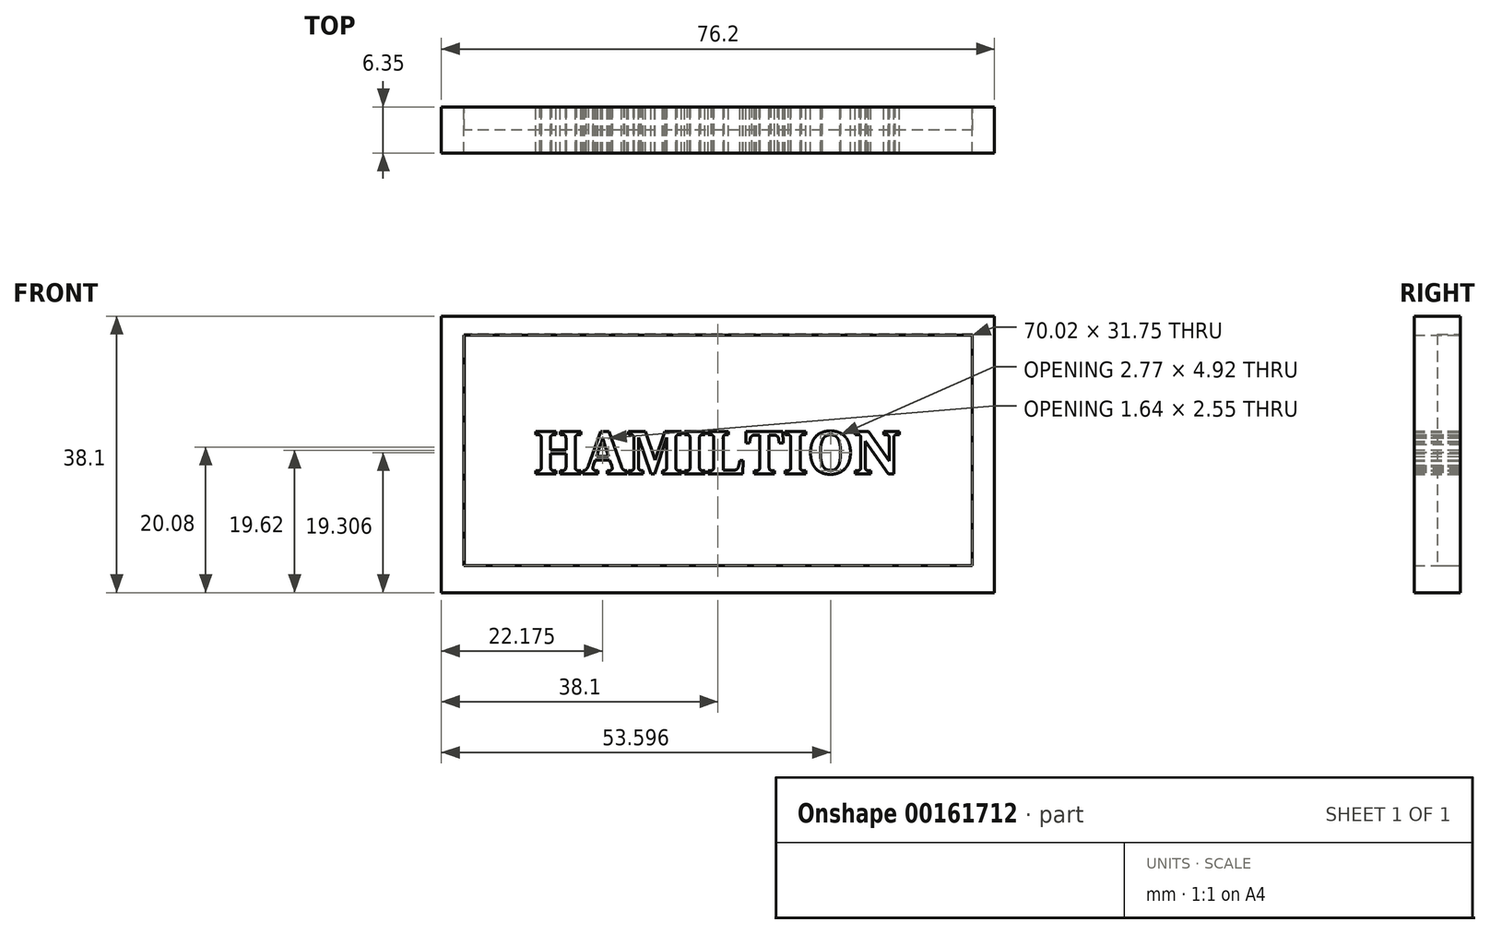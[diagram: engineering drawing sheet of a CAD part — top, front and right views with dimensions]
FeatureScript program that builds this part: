
annotation { "Feature Type Name" : "Feature", "Feature Type Description" : "" }
export const myFeature = defineFeature(function(context is Context, id is Id, definition is map)
    precondition{}
    {
        {
            var Q0;
            Q0=qCreatedBy(makeId("Front.planeOp"),FACE);
            var sketch = newSketch(context, id + "F0", { "sketchPlane" : qUnion([Q0])});
            skLineSegment(sketch, "E0.bottom", {"start": v(38.1, 19.05) * mm, "end": v(-38.1, 19.05) * mm});
            skLineSegment(sketch, "E0.top", {"start": v(38.1, -19.05) * mm, "end": v(-38.1, -19.05) * mm});
            skLineSegment(sketch, "E0.left", {"start": v(38.1, 19.05) * mm, "end": v(38.1, -19.05) * mm});
            skLineSegment(sketch, "E0.right", {"start": v(-38.1, 19.05) * mm, "end": v(-38.1, -19.05) * mm});
            skPoint(sketch, "E0.middle", {"position": v(0, 0) * mm});
            skText(sketch, "E1", { "text": "HAMILTION", "fontName": "NotoSerif-Bold.ttf"});
            skLineSegment(sketch, "E2.bottom", {"start": v(-35.01, 16.44) * mm, "end": v(35.01, 16.44) * mm});
            skLineSegment(sketch, "E2.top", {"start": v(-35.01, -15.3) * mm, "end": v(35.01, -15.3) * mm});
            skLineSegment(sketch, "E2.left", {"start": v(-35.01, 16.44) * mm, "end": v(-35.01, -15.3) * mm});
            skLineSegment(sketch, "E2.right", {"start": v(35.01, 16.44) * mm, "end": v(35.01, -15.3) * mm});
            skCircle(sketch, "E3", {"center": v(-30.43, 12.8) * mm, "radius": 2.29 * mm});
            skPoint(sketch, "E3.first.point", {"position": v(-32.08, 14.39) * mm});
            skPoint(sketch, "E3.second.point", {"position": v(-29.14, 10.9) * mm});
            skPoint(sketch, "E3.third.point", {"position": v(-30.06, 10.54) * mm});
            const initialGuessF0  = {"E1": [-0.02534, -0.00265, 1, 0, 0.00585]};
            skSetInitialGuess(sketch, initialGuessF0);
            skSolve(sketch);
        }
        {
            var Q0;
            Q0=makeQuery(id+"F0.imprint","IMPRINT",FACE,{"disambiguationData":[TD([[makeQuery(id+"F0.imprint","IMPRINT",EDGE,{"derivedFrom":sQuery(id+"F0.wireOp",EDGE,"E1.sketch_text.stroke-212")}),-1.0]])]});
            var Q1;
            Q1=makeQuery(id+"F0.imprint","IMPRINT",FACE,{"disambiguationData":[TD([[makeQuery(id+"F0.imprint","IMPRINT",EDGE,{"derivedFrom":sQuery(id+"F0.wireOp",EDGE,"E1.sketch_text.stroke-244")}),-1.0]])]});
            var Q2;
            Q2=makeQuery(id+"F0.imprint","IMPRINT",FACE,{"disambiguationData":[TD([[makeQuery(id+"F0.imprint","IMPRINT",EDGE,{"derivedFrom":sQuery(id+"F0.wireOp",EDGE,"E1.sketch_text.stroke-272")}),-1.0]])]});
            var Q3;
            Q3=makeQuery(id+"F0.imprint","IMPRINT",FACE,{"disambiguationData":[TD([[makeQuery(id+"F0.imprint","IMPRINT",EDGE,{"derivedFrom":sQuery(id+"F0.wireOp",EDGE,"E1.sketch_text.stroke-304")}),-1.0]])]});
            var Q4;
            Q4=makeQuery(id+"F0.imprint","IMPRINT",FACE,{"disambiguationData":[TD([[makeQuery(id+"F0.imprint","IMPRINT",EDGE,{"derivedFrom":sQuery(id+"F0.wireOp",EDGE,"E1.sketch_text.stroke-156")}),-1.0]])]});
            var Q5;
            Q5=makeQuery(id+"F0.imprint","IMPRINT",FACE,{"disambiguationData":[TD([[makeQuery(id+"F0.imprint","IMPRINT",EDGE,{"derivedFrom":sQuery(id+"F0.wireOp",EDGE,"E1.sketch_text.stroke-184")}),-1.0]])]});
            var Q6;
            Q6=makeQuery(id+"F0.imprint","IMPRINT",FACE,{"disambiguationData":[TD([[makeQuery(id+"F0.imprint","IMPRINT",EDGE,{"derivedFrom":sQuery(id+"F0.wireOp",EDGE,"E1.sketch_text.stroke-107")}),-1.0]])]});
            var Q7;
            Q7=makeQuery(id+"F0.imprint","IMPRINT",FACE,{"disambiguationData":[TD([[makeQuery(id+"F0.imprint","IMPRINT",EDGE,{"derivedFrom":sQuery(id+"F0.wireOp",EDGE,"E1.sketch_text.stroke-60")}),-1.0]])]});
            var Q8;
            Q8=makeQuery(id+"F0.imprint","IMPRINT",FACE,{"disambiguationData":[TD([[makeQuery(id+"F0.imprint","IMPRINT",EDGE,{"derivedFrom":sQuery(id+"F0.wireOp",EDGE,"E1.sketch_text.stroke-0")}),-1.0]])]});
            var Q9;
            Q9=makeQuery(id+"F0.imprint","IMPRINT",FACE,{"disambiguationData":[TD([[makeQuery(id+"F0.imprint","IMPRINT",EDGE,{"derivedFrom":sQuery(id+"F0.wireOp",EDGE,"E0.bottom")}),1.0]])]});
            extrude(context, id + "F1", {"entities" : qUnion([Q0, Q1, Q2, Q3, Q4, Q5, Q6, Q7, Q8, Q9]), "depth" : 6.35 * mm});
        }
        {
            var Q0;
            Q0=sQuery(id+"F0.wireOp",EDGE,"E3");
            extrude(context, id + "F2", {"bodyType" : ToolBodyType.SURFACE, "surfaceEntities" : qUnion([Q0]), "depth" : 0.86 * mm});
        }
        {
            var Q0;
            Q0=qCreatedBy(makeId("Front.planeOp"),FACE);
            var sketch = newSketch(context, id + "F3", { "sketchPlane" : qUnion([Q0])});
            skLineSegment(sketch, "E4.bottom", {"start": v(35.1, 16.57) * mm, "end": v(-34.95, 16.57) * mm});
            skLineSegment(sketch, "E4.top", {"start": v(35.1, -15.32) * mm, "end": v(-34.95, -15.32) * mm});
            skLineSegment(sketch, "E4.left", {"start": v(35.1, 16.57) * mm, "end": v(35.1, -15.32) * mm});
            skLineSegment(sketch, "E4.right", {"start": v(-34.95, 16.57) * mm, "end": v(-34.95, -15.32) * mm});
            skSolve(sketch);
        }
        {
            var Q0;
            Q0 = qSketchRegion(id + "F3", true);
            extrude(context, id + "F4", {"entities" : qUnion([Q0]), "depth" : 3.17 * mm});
        }
    });
